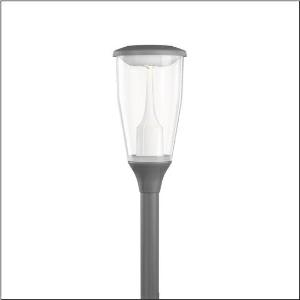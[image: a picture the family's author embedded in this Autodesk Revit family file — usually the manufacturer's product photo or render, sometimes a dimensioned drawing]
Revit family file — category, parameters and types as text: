
# Revit family: dl_11_iq___p1_0a_5xa5565ff14hp00022_87ad
name_source: partatom
category: Lighting Fixtures
units: mm (PartAtom-declared; Revit-internal decimal feet)

## family parameters
Cut with Voids When Loaded = No
Host = Face
Light Source = No
Part Type = Normal
Room Calculation Point = No
Round Connector Dimension = Use Diameter
Shared = No

## types (1)
- --- (1 x LED, 4780 lm, 33.6 W, 3000K)
    Apparent Load = 34 VA
    CIE Flux Codes = 23 60 93 95 100
    Color Rendering = 70
    Color Temperature = 3000K
    Default Elevation = 1800 mm
    Description = DL 11 iQ, mast luminaire, Module 540 iQ-SR, primary light control with 3 zone facetted reflector, of plastic, silver coated, highly specular, structured, primary optical cover: cover, of PMMA, transparent, light distribution: P1.0a, light emission: direct distribution, primary light characteristic: asymmetric, installation type: post-top, LED, High Power LED, light colour: 730, colour temperature: 3000K, control: Street-Remote, Auto-Match, Temp-Guard, Lumen-Switch, Night-Set, Smart-Wire, Light-Fading, Desk-Remote (wireless, voltage-free reading and setting of iQ features in the workshop via application-optimized NFC function/RFID function), optimised constant luminous flux control (CLO 2.0), mains connection: 220..240V, AC, 50/60Hz, connection cable pre-assembled, cable length: 5,5m, start of lifetime: 34W, end of service life: 36W, luminaire housing, upper part, of diecast aluminium, coated, Siteco® metallic grey (DB 702S), spigot size: 60mm (post-top), post-top mast mounting element, of diecast aluminium, coated, Siteco® metallic grey (DB 702S), Module 540 iQ-SR, traffic white (RAL 9016), equipment: Power, protection rating (complete): IP66, insulation class (complete): insulation class II (safety insulation), certification: CE, ENEC, ENEC+, VDE, packaging unit: 1 piece

Light Distribution: P1.0a
    Height = 665 mm
    Lamp = 1 x LED
    Lamp Light Flux = 4780 lm
    Lamp Power = 33.6 W
    Lamp count = 1
    Length = 334 mm
    Luminous efficacy = 142 lm/W
    Manufacturer = Siteco
    ModVariant = No
    Model = 5XA5565FF14HP00022
    Number of Poles = 1
    OnlyDefault = Yes
    Power Factor = 1
    Product Name = DL 11 iQ | P1.0a
    Product group = mast luminaire | pylon top
    ProductGroupID = 6100
    Protection Class = Protection class II
    Protection Degree = IP 66
    RLX_Detail_Level = 1
    RLX_Emergency_Light_Flux = 0 lm
    RLX_Emergency_Type = 0
    RLX_Emergency_Type_DB = No
    RlxData = <blob elided: 104401 chars, md5=6ec4a181>
    Socket = socket
    Standby Power = 0 W
    System Light Flux = 4780 lm
    System Power = 34 W
    Type Comments = factory setting: luminous flux: 100 % | dim-lin: 254 | 695 mA
    Type Image = l_1258354.jpg
    URL = http://relux.com
    VarID = @adj_021973
    Voltage = 0 V
    Weight = 0.00 kg
    Width = 0 mm  [stored 0 ft]

note: [stored X ft] marks values corroborated as IEEE doubles in the binary element streams (Revit-internal decimal feet)

## geometry (parser evidence)
native form markers: Blend x4, Sweep x12
no freeform markers — native parametric forms only
